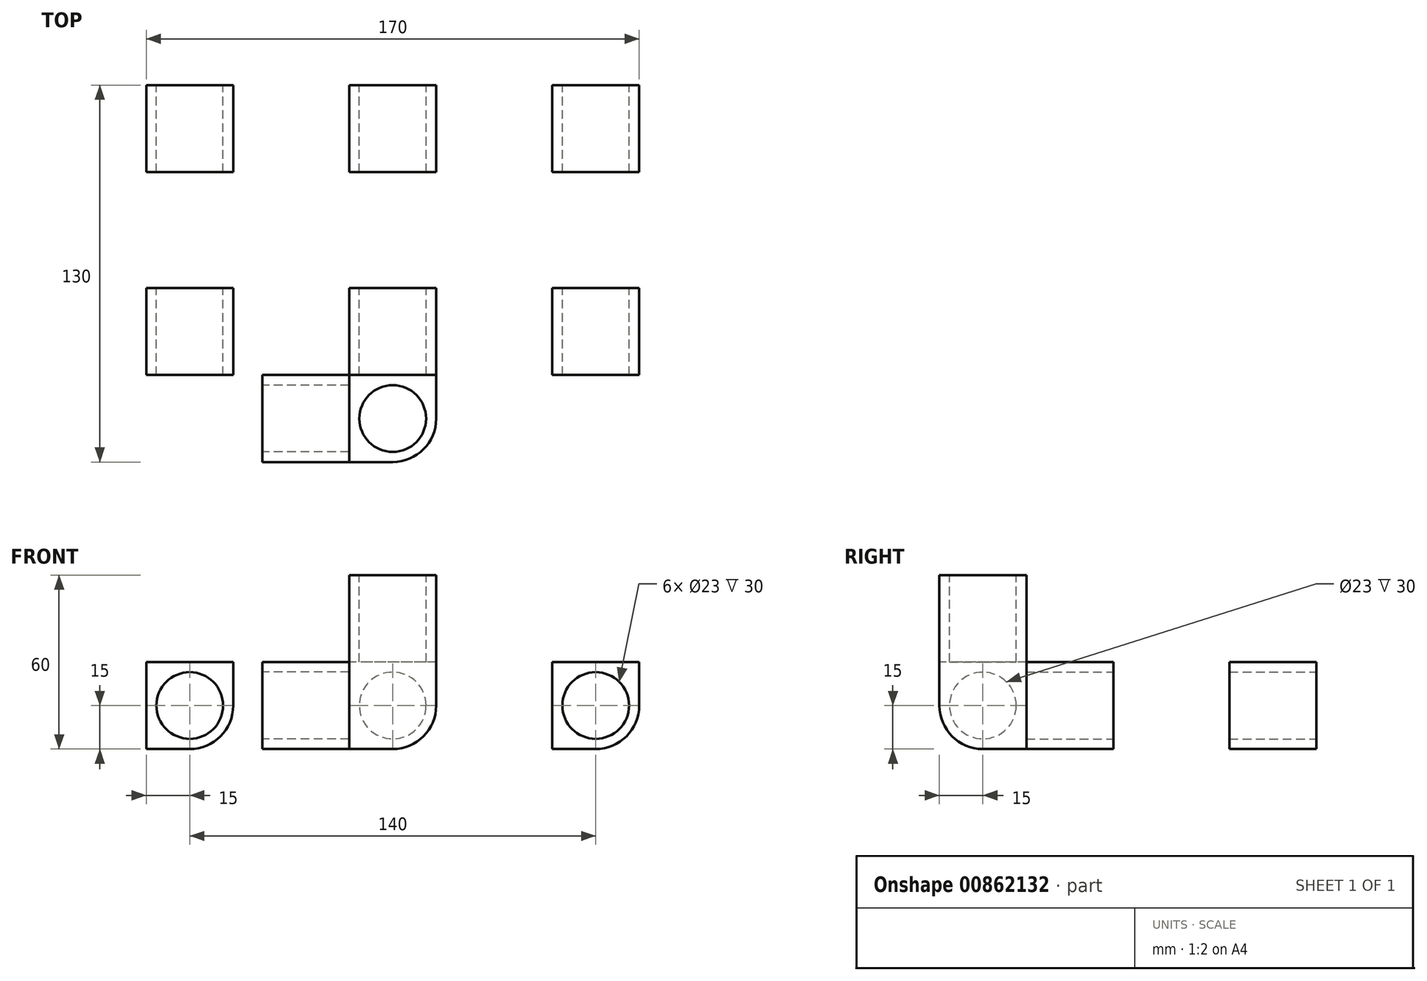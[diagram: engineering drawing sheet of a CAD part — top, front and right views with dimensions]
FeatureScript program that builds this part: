
annotation { "Feature Type Name" : "Feature", "Feature Type Description" : "" }
export const myFeature = defineFeature(function(context is Context, id is Id, definition is map)
    precondition{}
    {
        {
            var Q0;
            Q0=qCreatedBy(makeId("Top.planeOp"),FACE);
            var sketch = newSketch(context, id + "F0", { "sketchPlane" : qUnion([Q0])});
            skLineSegment(sketch, "E0", {"start": v(0, 0) * mm, "end": v(0, 30) * mm});
            skLineSegment(sketch, "E1", {"start": v(0, 30) * mm, "end": v(30, 30) * mm});
            skLineSegment(sketch, "E2", {"start": v(30, 30) * mm, "end": v(30, -30) * mm});
            skLineSegment(sketch, "E3", {"start": v(30, -30) * mm, "end": v(-30, -30) * mm});
            skLineSegment(sketch, "E4", {"start": v(-30, -30) * mm, "end": v(-30, 0) * mm});
            skLineSegment(sketch, "E5", {"start": v(-30, 0) * mm, "end": v(0, 0) * mm});
            skLineSegment(sketch, "E6", {"start": v(0, 0) * mm, "end": v(0, -30) * mm});
            skLineSegment(sketch, "E7", {"start": v(30, 0) * mm, "end": v(0, 0) * mm});
            skSolve(sketch);
        }
        {
            var Q0;
            {var subQ0=sQuery(id+"F0.wireOp",EDGE,"E4");Q0=makeQuery(id+"F0.imprint","IMPRINT",FACE,{"disambiguationData":[TD([[makeQuery(id+"F0.imprint","IMPRINT",EDGE,{"derivedFrom":subQ0}),-1.0]])]});}
            var Q1;
            Q1=makeQuery(id+"F0.imprint","IMPRINT",FACE,{"disambiguationData":[TD([[makeQuery(id+"F0.imprint","IMPRINT",EDGE,{"derivedFrom":sQuery(id+"F0.wireOp",EDGE,"E0")}),-1.0]])]});
            extrude(context, id + "F1", {"entities" : qUnion([Q0, Q1]), "depth" : 30 * mm, "offsetDistance" : 25 * mm});
        }
        {
            var Q0;
            {var subQ4=sQuery(id+"F0.wireOp",EDGE,"E6");Q0=makeQuery(id+"F0.imprint","IMPRINT",FACE,{"disambiguationData":[TD([[makeQuery(id+"F0.imprint","IMPRINT",EDGE,{"derivedFrom":subQ4}),1.0]])]});}
            extrude(context, id + "F2", {"entities" : qUnion([Q0]), "depth" : 60 * mm, "offsetDistance" : 25 * mm});
        }
        {
            var Q0;
            Q0=makeQuery(id+"F2.opExtrude","CAP_FACE",FACE,{"disambiguationData":[OSD([sQuery(id+"F0.wireOp",EDGE,"E2"),sQuery(id+"F0.wireOp",EDGE,"E3"),sQuery(id+"F0.wireOp",EDGE,"E6"),sQuery(id+"F0.wireOp",EDGE,"E7")])],"isStart":false});
            var sketch = newSketch(context, id + "F3", { "sketchPlane" : qUnion([Q0])});
            skCircle(sketch, "E8", {"center": v(15, -15) * mm, "radius": 11.5 * mm});
            skPoint(sketch, "E8.centerSnap0", {"position": v(0, -15) * mm});
            skPoint(sketch, "E8.centerSnap1", {"position": v(15, 0) * mm});
            skSolve(sketch);
        }
        {
            var Q0;
            Q0=makeQuery(id+"F1.opExtrude","SWEPT_FACE",FACE,{"disambiguationData":[OSD([sQuery(id+"F0.wireOp",EDGE,"E1")])]});
            var sketch = newSketch(context, id + "F4", { "sketchPlane" : qUnion([Q0])});
            skCircle(sketch, "E9", {"center": v(-15, 15) * mm, "radius": 11.5 * mm});
            skPoint(sketch, "E9.centerSnap0", {"position": v(0, 15) * mm});
            skPoint(sketch, "E9.centerSnap1", {"position": v(-15, 30) * mm});
            skSolve(sketch);
        }
        {
            var Q0;
            Q0=makeQuery(id+"F1.opExtrude","SWEPT_FACE",FACE,{"disambiguationData":[OSD([sQuery(id+"F0.wireOp",EDGE,"E4")])]});
            var sketch = newSketch(context, id + "F5", { "sketchPlane" : qUnion([Q0])});
            skCircle(sketch, "E10", {"center": v(15, 15) * mm, "radius": 11.5 * mm});
            skPoint(sketch, "E10.centerSnap0", {"position": v(0, 15) * mm});
            skPoint(sketch, "E10.centerSnap1", {"position": v(15, 30) * mm});
            skSolve(sketch);
        }
        {
            var Q0;
            Q0=makeQuery(id+"F4.imprint","IMPRINT",FACE,{"disambiguationData":[TD([[makeQuery(id+"F4.imprint","IMPRINT",EDGE,{"derivedFrom":sQuery(id+"F4.wireOp",EDGE,"E9")}),1.0]])]});
            extrude(context, id + "F6", {"entities" : qUnion([Q0]), "operationType" : NewBodyOperationType.REMOVE, "oppositeDirection" : true, "depth" : 30 * mm, "offsetDistance" : 25 * mm});
        }
        {
            var Q0;
            Q0=makeQuery(id+"F5.imprint","IMPRINT",FACE,{"disambiguationData":[TD([[makeQuery(id+"F5.imprint","IMPRINT",EDGE,{"derivedFrom":sQuery(id+"F5.wireOp",EDGE,"E10")}),1.0]])]});
            extrude(context, id + "F7", {"entities" : qUnion([Q0]), "operationType" : NewBodyOperationType.REMOVE, "oppositeDirection" : true, "depth" : 30 * mm, "offsetDistance" : 25 * mm});
        }
        {
            var Q0;
            Q0=makeQuery(id+"F3.imprint","IMPRINT",FACE,{"disambiguationData":[TD([[makeQuery(id+"F3.imprint","IMPRINT",EDGE,{"derivedFrom":sQuery(id+"F3.wireOp",EDGE,"E8")}),1.0]])]});
            extrude(context, id + "F8", {"entities" : qUnion([Q0]), "operationType" : NewBodyOperationType.REMOVE, "oppositeDirection" : true, "depth" : 30 * mm, "offsetDistance" : 25 * mm});
        }
        {
            var Q0;
            Q0=makeQuery(id+"F2.opExtrude","CAP_EDGE",EDGE,{"disambiguationData":[OSD([sQuery(id+"F0.wireOp",EDGE,"E3")])],"isStart":true});
            var Q1;
            Q1=makeQuery(id+"F2.opExtrude","CAP_EDGE",EDGE,{"disambiguationData":[OSD([sQuery(id+"F0.wireOp",EDGE,"E2")])],"isStart":true});
            var Q2;
            Q2=makeQuery(id+"F2.opExtrude","SWEPT_EDGE",EDGE,{"disambiguationData":[OSD([sQuery(id+"F0.wireOp",EDGE,"E2"),sQuery(id+"F0.wireOp",EDGE,"E3")])]});
            var Q3;
            Q3=makeQuery(id+"F1.opExtrude","CAP_EDGE",EDGE,{"disambiguationData":[OSD([sQuery(id+"F0.wireOp",EDGE,"E3")])],"isStart":true});
            var Q4;
            Q4=makeQuery(id+"F1.opExtrude","CAP_EDGE",EDGE,{"disambiguationData":[OSD([sQuery(id+"F0.wireOp",EDGE,"E2")])],"isStart":true});
            fillet(context, id + "F9", {"entities" : qUnion([Q0, Q1, Q2, Q3, Q4]), "radius" : 15 * mm, "tangentPropagation" : true, "allowEdgeOverflow" : false});
        }
        {
            var Q0;
            Q0=makeQuery(id+"F1.opExtrude","SWEPT_BODY",BODY,{"disambiguationData":[OSD([sQuery(id+"F0.wireOp",EDGE,"E0"),sQuery(id+"F0.wireOp",EDGE,"E1"),sQuery(id+"F0.wireOp",EDGE,"E2"),sQuery(id+"F0.wireOp",EDGE,"E7")])]});
            transform(context, id + "F10", {"entities" : qUnion([Q0]), "transformType" : TransformType.TRANSLATION_3D, "dx" : 0 * mm, "dy" : 70 * mm, "dz" : 0 * mm, "makeCopy" : true});
        }
        {
            var Q0;
            Q0=makeQuery(id+"F1.opExtrude","SWEPT_BODY",BODY,{"disambiguationData":[OSD([sQuery(id+"F0.wireOp",EDGE,"E0"),sQuery(id+"F0.wireOp",EDGE,"E1"),sQuery(id+"F0.wireOp",EDGE,"E2"),sQuery(id+"F0.wireOp",EDGE,"E7")])]});
            transform(context, id + "F11", {"entities" : qUnion([Q0]), "transformType" : TransformType.TRANSLATION_3D, "dx" : 70 * mm, "dy" : 0 * mm, "dz" : 0 * mm, "makeCopy" : true});
        }
        {
            var Q0;
            Q0=makeQuery(id+"F1.opExtrude","SWEPT_BODY",BODY,{"disambiguationData":[OSD([sQuery(id+"F0.wireOp",EDGE,"E0"),sQuery(id+"F0.wireOp",EDGE,"E1"),sQuery(id+"F0.wireOp",EDGE,"E2"),sQuery(id+"F0.wireOp",EDGE,"E7")])]});
            transform(context, id + "F12", {"entities" : qUnion([Q0]), "transformType" : TransformType.TRANSLATION_3D, "dx" : 70 * mm, "dy" : 70 * mm, "dz" : 0 * mm, "makeCopy" : true});
        }
        {
            var Q0;
            Q0=makeQuery(id+"F1.opExtrude","SWEPT_BODY",BODY,{"disambiguationData":[OSD([sQuery(id+"F0.wireOp",EDGE,"E0"),sQuery(id+"F0.wireOp",EDGE,"E1"),sQuery(id+"F0.wireOp",EDGE,"E2"),sQuery(id+"F0.wireOp",EDGE,"E7")])]});
            transform(context, id + "F13", {"entities" : qUnion([Q0]), "transformType" : TransformType.TRANSLATION_3D, "dx" : -70 * mm, "dy" : 0 * mm, "dz" : 0 * mm, "makeCopy" : true});
        }
        {
            var Q0;
            Q0=makeQuery(id+"F1.opExtrude","SWEPT_BODY",BODY,{"disambiguationData":[OSD([sQuery(id+"F0.wireOp",EDGE,"E0"),sQuery(id+"F0.wireOp",EDGE,"E1"),sQuery(id+"F0.wireOp",EDGE,"E2"),sQuery(id+"F0.wireOp",EDGE,"E7")])]});
            transform(context, id + "F14", {"entities" : qUnion([Q0]), "transformType" : TransformType.TRANSLATION_3D, "dx" : -70 * mm, "dy" : 70 * mm, "dz" : 0 * mm, "makeCopy" : true});
        }
    });
